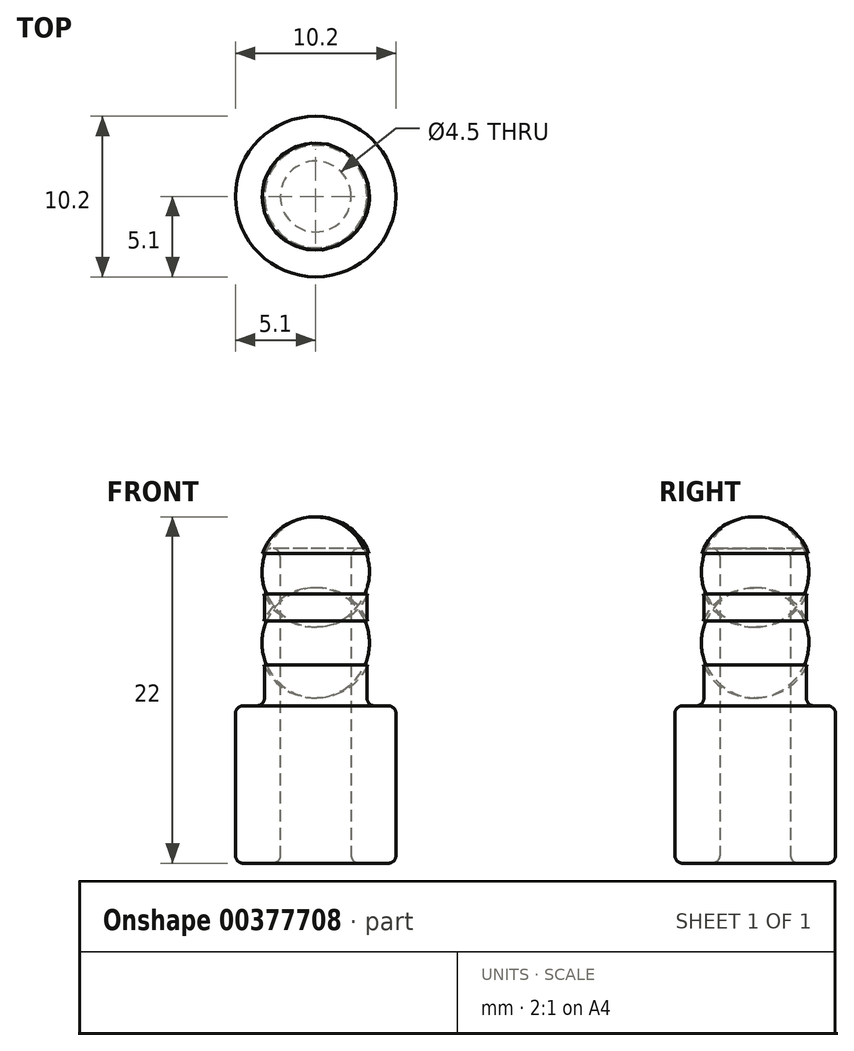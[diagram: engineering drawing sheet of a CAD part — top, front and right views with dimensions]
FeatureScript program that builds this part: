
annotation { "Feature Type Name" : "Feature", "Feature Type Description" : "" }
export const myFeature = defineFeature(function(context is Context, id is Id, definition is map)
    precondition{}
    {
        {
            var Q0;
            Q0=qCreatedBy(makeId("Top.planeOp"),FACE);
            var sketch = newSketch(context, id + "F0", { "sketchPlane" : qUnion([Q0])});
            skCircle(sketch, "E0", {"center": v(0, 0) * mm, "radius": 5.1 * mm});
            skCircle(sketch, "E1", {"center": v(0, 0) * mm, "radius": 3.25 * mm});
            skCircle(sketch, "E2", {"center": v(0, 0) * mm, "radius": 2.25 * mm});
            skSolve(sketch);
        }
        {
            var Q0;
            Q0=makeQuery(id+"F0.imprint","IMPRINT",FACE,{"disambiguationData":[TD([[makeQuery(id+"F0.imprint","IMPRINT",EDGE,{"derivedFrom":sQuery(id+"F0.wireOp",EDGE,"E1")}),1.0]])]});
            extrude(context, id + "F1", {"entities" : qUnion([Q0]), "depth" : 20 * mm});
        }
        {
            var Q0;
            Q0=makeQuery(id+"F0.imprint","IMPRINT",FACE,{"disambiguationData":[TD([[makeQuery(id+"F0.imprint","IMPRINT",EDGE,{"derivedFrom":sQuery(id+"F0.wireOp",EDGE,"E0")}),1.0]])]});
            extrude(context, id + "F2", {"entities" : qUnion([Q0]), "operationType" : NewBodyOperationType.ADD, "depth" : 10 * mm});
        }
        {
            var Q0;
            Q0=qCreatedBy(makeId("Front.planeOp"),FACE);
            var sketch = newSketch(context, id + "F3", { "sketchPlane" : qUnion([Q0])});
            skArc(sketch, "E3", {"start": v(3.25, 17) * mm, "mid": v(3.59, 18.5) * mm, "end": v(3.25, 20) * mm});
            skLineSegment(sketch, "E4", {"start": v(3.25, 20) * mm, "end": v(3.25, 17) * mm});
            skArc(sketch, "E5", {"start": v(3.25, 12.5) * mm, "mid": v(3.59, 14) * mm, "end": v(3.25, 15.5) * mm});
            skLineSegment(sketch, "E6", {"start": v(3.25, 15.5) * mm, "end": v(3.25, 12.5) * mm});
            skLineSegment(sketch, "E7", {"start": v(0, 0) * mm, "end": v(0, 28.28) * mm});
            skSolve(sketch);
        }
        {
            var Q0;
            Q0=makeQuery(id+"F3.imprint","IMPRINT",FACE,{"disambiguationData":[TD([[makeQuery(id+"F3.imprint","IMPRINT",EDGE,{"derivedFrom":sQuery(id+"F3.wireOp",EDGE,"E3")}),1.0]])]});
            var Q1;
            Q1=makeQuery(id+"F3.imprint","IMPRINT",FACE,{"disambiguationData":[TD([[makeQuery(id+"F3.imprint","IMPRINT",EDGE,{"derivedFrom":sQuery(id+"F3.wireOp",EDGE,"E5")}),1.0]])]});
            var Q2;
            Q2=sQuery(id+"F3.wireOp",EDGE,"E7");
            revolve(context, id + "F4", {"operationType" : NewBodyOperationType.ADD, "entities" : qUnion([Q0, Q1]), "axis" : qUnion([Q2]), "revolveType" : RevolveType.FULL});
        }
        {
            var Q0;
            Q0=makeQuery(id+"F2.opExtrude","CAP_FACE",FACE,{"disambiguationData":[OSD([sQuery(id+"F0.wireOp",EDGE,"E0"),sQuery(id+"F0.wireOp",EDGE,"E1")])],"isStart":false});
            var Q1;
            Q1=makeQuery(id+"F4.opRevolve","SWEPT_FACE",FACE,{"disambiguationData":[OSD([sQuery(id+"F3.wireOp",EDGE,"E3")])]});
            var Q2;
            Q2=makeQuery(id+"F2.opExtrude","CAP_EDGE",EDGE,{"disambiguationData":[OSD([sQuery(id+"F0.wireOp",EDGE,"E1")])],"isStart":false});
            var Q3;
            Q3=makeQuery(id+"F1.opExtrude","CAP_EDGE",EDGE,{"disambiguationData":[OSD([sQuery(id+"F0.wireOp",EDGE,"E2")])],"isStart":false});
            var Q4;
            Q4=makeQuery(id+"F1.opExtrude","CAP_FACE",FACE,{"disambiguationData":[OSD([sQuery(id+"F0.wireOp",EDGE,"E1"),sQuery(id+"F0.wireOp",EDGE,"E2")])],"isStart":false});
            var Q5;
            Q5=makeQuery(id+"F1.opExtrude","SWEPT_FACE",FACE,{"disambiguationData":[OSD([sQuery(id+"F0.wireOp",EDGE,"E2")])]});
            var Q6;
            Q6=makeQuery(id+"F4.opRevolve","SWEPT_FACE",FACE,{"disambiguationData":[OSD([sQuery(id+"F3.wireOp",EDGE,"E5")])]});
            var Q7;
            Q7=makeQuery(id+"F2.opExtrude","CAP_EDGE",EDGE,{"disambiguationData":[OSD([sQuery(id+"F0.wireOp",EDGE,"E0")])],"isStart":false});
            var Q8;
            Q8=makeQuery(id+"F2.opExtrude","SWEPT_FACE",FACE,{"disambiguationData":[OSD([sQuery(id+"F0.wireOp",EDGE,"E0")])]});
            var Q9;
            {var subQ0=sQuery(id+"F3.wireOp",EDGE,"E4");var subQ1=sQuery(id+"F3.wireOp",EDGE,"E3");Q9=makeQuery(id+"F4.boolean.opBoolean","MERGE",EDGE,{"derivedFrom":[makeQuery(id+"F1.opExtrude","CAP_EDGE",EDGE,{"disambiguationData":[OSD([sQuery(id+"F0.wireOp",EDGE,"E1")])],"isStart":false}),makeQuery(id+"F4.opRevolve","SWEPT_EDGE",EDGE,{"disambiguationData":[OSD([subQ1,subQ0]),TDD([makeQuery(id+"F3.imprint","INTERSECT",VERTEX,{"disambiguationData":[OD(1.0)],"derivedFrom":[subQ1,subQ0]})])]})]});}
            var Q10;
            {var subQ0=sQuery(id+"F0.wireOp",EDGE,"E1");Q10=makeQuery(id+"F4.boolean.opBoolean","SPLIT",FACE,{"disambiguationData":[TD([makeQuery(id+"F2.opExtrude","CAP_FACE",FACE,{"disambiguationData":[OSD([sQuery(id+"F0.wireOp",EDGE,"E0"),subQ0])],"isStart":false})])],"derivedFrom":makeQuery(id+"F1.opExtrude","SWEPT_FACE",FACE,{"disambiguationData":[OSD([subQ0])]})});}
            var Q11;
            {var subQ0=sQuery(id+"F3.wireOp",EDGE,"E4");var subQ1=sQuery(id+"F3.wireOp",EDGE,"E3");Q11=makeQuery(id+"F4.opRevolve","SWEPT_EDGE",EDGE,{"disambiguationData":[OSD([subQ1,subQ0]),TDD([makeQuery(id+"F3.imprint","INTERSECT",VERTEX,{"disambiguationData":[OD(0.0)],"derivedFrom":[subQ1,subQ0]})])]});}
            var Q12;
            Q12=makeQuery(id+"F4.boolean.opBoolean","SPLIT",FACE,{"disambiguationData":[TD([makeQuery(id+"F4.opRevolve","SWEPT_FACE",FACE,{"disambiguationData":[OSD([sQuery(id+"F3.wireOp",EDGE,"E3")])]})])],"derivedFrom":makeQuery(id+"F1.opExtrude","SWEPT_FACE",FACE,{"disambiguationData":[OSD([sQuery(id+"F0.wireOp",EDGE,"E1")])]})});
            var Q13;
            {var subQ0=sQuery(id+"F3.wireOp",EDGE,"E6");var subQ1=sQuery(id+"F3.wireOp",EDGE,"E5");Q13=makeQuery(id+"F4.opRevolve","SWEPT_EDGE",EDGE,{"disambiguationData":[OSD([subQ1,subQ0]),TDD([makeQuery(id+"F3.imprint","INTERSECT",VERTEX,{"disambiguationData":[OD(0.0)],"derivedFrom":[subQ1,subQ0]})])]});}
            var Q14;
            {var subQ0=sQuery(id+"F3.wireOp",EDGE,"E6");var subQ1=sQuery(id+"F3.wireOp",EDGE,"E5");Q14=makeQuery(id+"F4.opRevolve","SWEPT_EDGE",EDGE,{"disambiguationData":[OSD([subQ1,subQ0]),TDD([makeQuery(id+"F3.imprint","INTERSECT",VERTEX,{"disambiguationData":[OD(1.0)],"derivedFrom":[subQ1,subQ0]})])]});}
            var Q15;
            Q15=makeQuery(id+"F1.opExtrude","CAP_EDGE",EDGE,{"disambiguationData":[OSD([sQuery(id+"F0.wireOp",EDGE,"E2")])],"isStart":true});
            var Q16;
            {var subQ0=sQuery(id+"F0.wireOp",EDGE,"E1");Q16=makeQuery(id+"F2.boolean.opBoolean","MERGE",FACE,{"derivedFrom":[makeQuery(id+"F1.opExtrude","CAP_FACE",FACE,{"disambiguationData":[OSD([subQ0,sQuery(id+"F0.wireOp",EDGE,"E2")])],"isStart":true}),makeQuery(id+"F2.opExtrude","CAP_FACE",FACE,{"disambiguationData":[OSD([sQuery(id+"F0.wireOp",EDGE,"E0"),subQ0])],"isStart":true})]});}
            var Q17;
            Q17=makeQuery(id+"F2.opExtrude","CAP_EDGE",EDGE,{"disambiguationData":[OSD([sQuery(id+"F0.wireOp",EDGE,"E0")])],"isStart":true});
            fillet(context, id + "F5", {"entities" : qUnion([Q0, Q1, Q2, Q3, Q4, Q5, Q6, Q7, Q8, Q9, Q10, Q11, Q12, Q13, Q14, Q15, Q16, Q17]), "radius" : 0.5 * mm, "tangentPropagation" : true, "allowEdgeOverflow" : false});
        }
    });
